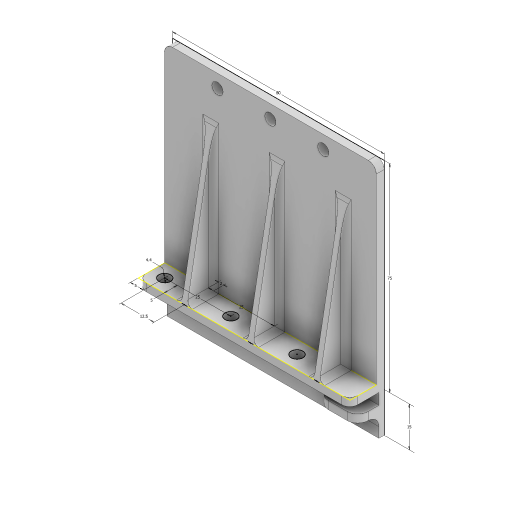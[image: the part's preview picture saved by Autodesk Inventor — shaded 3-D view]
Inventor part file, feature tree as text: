
AUTODESK INVENTOR PART (.ipt)
format: ipt  version: 2023 (Build 270158000, 158)  size: 264,704 bytes
history: native  units: mm
features: sketch x6, extrude x6, fillet x4, loft x1, pattern_linear x1, projected_geometry x1
ambient origin geometry x8: Origin, YZ Plane, XZ Plane, XY Plane, X Axis, Y Axis, Z Axis, Center Point
bodies: Solid1 (feature_tree)
feature tree (19):
  sketch  "Sketch1"  dims[d0=80.0mm d1=75.0mm]
  extrude  "Extrusion1"  Depth=75.0mm
  extrude  "Extrusion2"  Depth=3.0mm TaperAngle=0.0deg
  extrude  "Extrusion3"  Depth=3.0mm
  sketch  "Sketch3"  dims[d5=2.0mm d6=0.0mm d7=3.0mm]
  loft  "Loft1"
  pattern_linear  "Rectangular Pattern1"  Count1=3 Spacing1=25.0mm
  extrude  "Extrusion4"  Depth=2.0mm
  extrude  "Extrusion5"  Depth=4.0mm
  fillet  "Fillet1"  Radius=10.0mm
  fillet  "Fillet2"  Radius=55.0mm
  fillet  "Fillet3"  [1 undecoded]
  extrude  "Extrusion6"  TaperAngle=0.0deg  [1 undecoded]
  fillet  "Fillet4"  Radius=30.0mm
  sketch  "Sketch2"  dims[d2=15.0mm d3=3.0mm d4=0.0mm]
  projected_geometry  "Projected Loop1"
  sketch  "Sketch4"  dims[d8=10.0mm d9=0.0mm d10=4.4mm]
  sketch  "Sketch5"  dims[d11=5.0mm]
  sketch  "Sketch6"  dims[d12=5.0mm d13=30.0mm d15=25.0mm d16=10.0mm d18=10.0mm d20=2.0mm d21=12.5mm d22=30.0mm d24=25.0mm d25=10.0mm d27=10.0mm d29=55.0mm d30=0.0mm d31=90.0deg d32=0.0mm d33=90.0deg d34=30.0mm d36=25.0mm d37=0.0mm d38=0.0mm d39=4.2mm d40=70.0mm d41=20.0mm d42=30.0mm d44=20.0mm d45=10.0mm d47=10.0mm d49=0.0mm d50=0.0mm d51=3.0mm d52=10.0mm d53=2.0mm d54=15.0mm d55=3.0mm d56=4.175mm d57=8.0mm d58=0.0mm d59=4.0mm]
note: 2 required parameter values undecoded (feature->parameter linkage not recoverable at this tier; creation-order binding heuristic only, values carry confidence <= 0.55)
